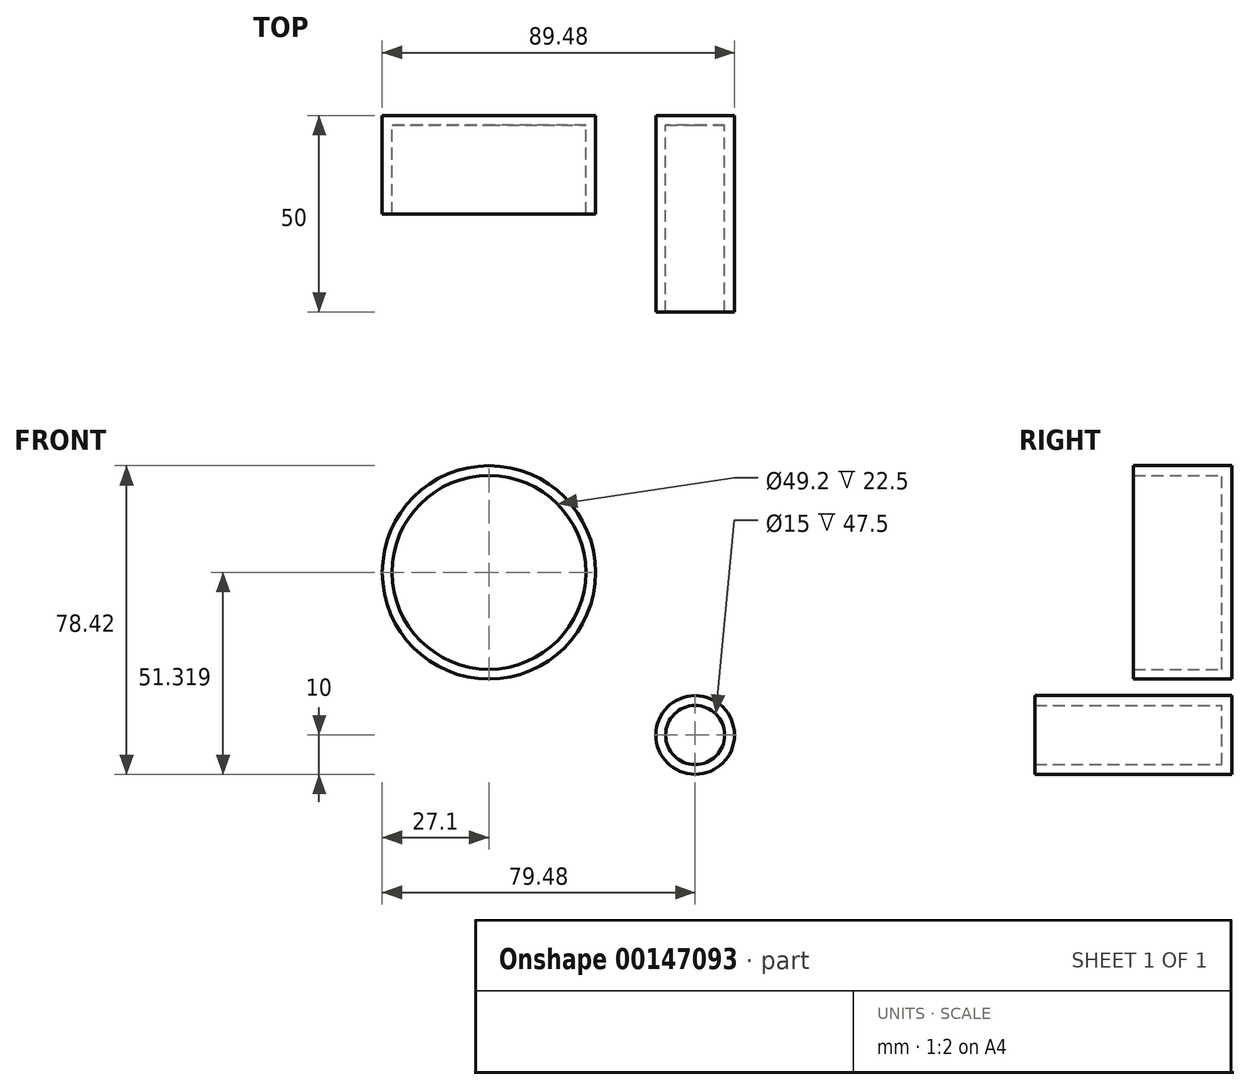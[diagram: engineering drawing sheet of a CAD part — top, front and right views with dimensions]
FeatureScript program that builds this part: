
annotation { "Feature Type Name" : "Feature", "Feature Type Description" : "" }
export const myFeature = defineFeature(function(context is Context, id is Id, definition is map)
    precondition{}
    {
        {
            var Q0;
            Q0=qCreatedBy(makeId("Front.planeOp"),FACE);
            var sketch = newSketch(context, id + "F5", { "sketchPlane" : qUnion([Q0])});
            skCircle(sketch, "E0", {"center": v(0, 0) * mm, "radius": 10 * mm});
            skSolve(sketch);
        }
        {
            var Q0;
            Q0 = qSketchRegion(id + "F5", true);
            extrude(context, id + "F0", {"entities" : qUnion([Q0]), "depth" : 50 * mm});
        }
        {
            var Q0;
            Q0=qCreatedBy(makeId("Front.planeOp"),FACE);
            var sketch = newSketch(context, id + "F1", { "sketchPlane" : qUnion([Q0])});
            skCircle(sketch, "E1", {"center": v(-52.38, 41.32) * mm, "radius": 27.1 * mm});
            skSolve(sketch);
        }
        {
            var Q0;
            Q0 = qSketchRegion(id + "F1", true);
            extrude(context, id + "F2", {"entities" : qUnion([Q0]), "depth" : 25 * mm});
        }
        {
            var Q0;
            Q0=makeQuery(id+"F0.opExtrude","CAP_FACE",FACE,{"disambiguationData":[OSD([sQuery(id+"F5.wireOp",EDGE,"E0")])],"isStart":false});
            shell(context, id + "F3", {"entities" : qUnion([Q0]), "thickness" : 2.5 * mm});
        }
        {
            var Q0;
            Q0=makeQuery(id+"F2.opExtrude","CAP_FACE",FACE,{"disambiguationData":[OSD([sQuery(id+"F1.wireOp",EDGE,"E1")])],"isStart":false});
            shell(context, id + "F4", {"entities" : qUnion([Q0]), "thickness" : 2.5 * mm});
        }
    });
